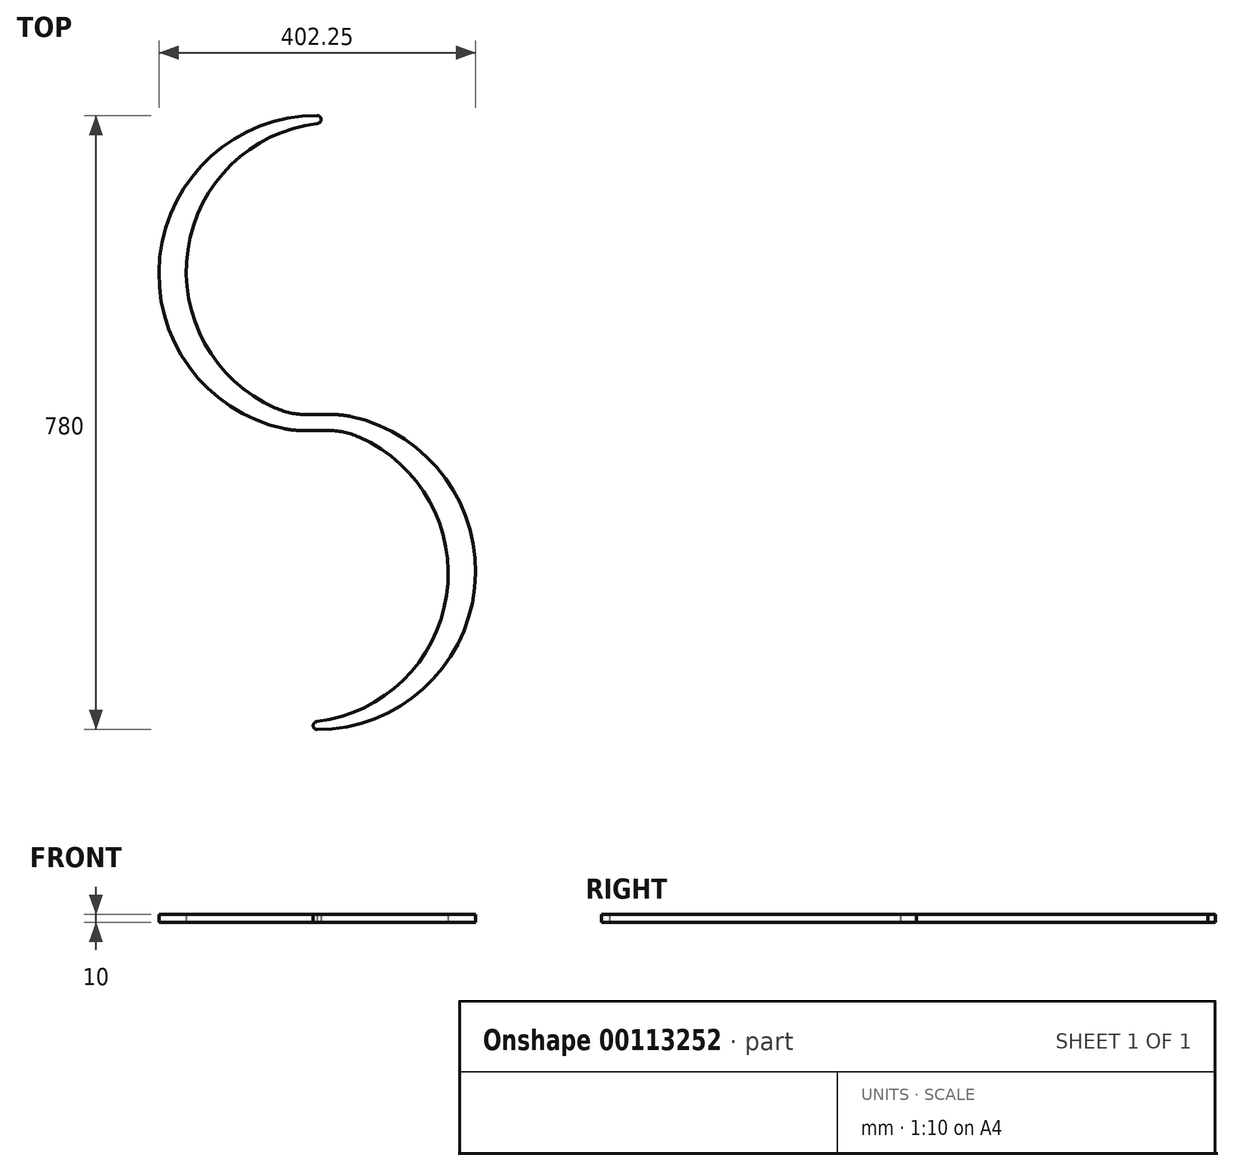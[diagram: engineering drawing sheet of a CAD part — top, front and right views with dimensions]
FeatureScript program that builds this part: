
annotation { "Feature Type Name" : "Feature", "Feature Type Description" : "" }
export const myFeature = defineFeature(function(context is Context, id is Id, definition is map)
    precondition{}
    {
        {
            var Q0;
            Q0=qCreatedBy(makeId("Top.planeOp"),FACE);
            var sketch = newSketch(context, id + "F0", { "sketchPlane" : qUnion([Q0])});
            skArc(sketch, "E0", {"start": v(0, 390) * mm, "mid": v(-200, 210.09) * mm, "end": v(-42.2, -7.78) * mm});
            skLineSegment(sketch, "E1", {"start": v(-21.21, -10) * mm, "end": v(0, -10) * mm});
            skLineSegment(sketch, "E2", {"start": v(0, -10) * mm, "end": v(0, 10) * mm, "construction": true});
            skPoint(sketch, "E3", {"position": v(0, 0) * mm});
            skLineSegment(sketch, "E4", {"start": v(0, 10) * mm, "end": v(-12.94, 10) * mm});
            skArc(sketch, "E5", {"start": v(0, 380) * mm, "mid": v(-164.3, 219.56) * mm, "end": v(-53.31, 18.51) * mm});
            skArc(sketch, "E6", {"start": v(0, 380) * mm, "mid": v(5, 385) * mm, "end": v(0, 390) * mm});
            skArc(sketch, "E7.1.0", {"start": v(0, -390) * mm, "mid": v(200, -210.09) * mm, "end": v(42.2, 7.78) * mm});
            skArc(sketch, "E7.1.1", {"start": v(0, -380) * mm, "mid": v(164.3, -219.56) * mm, "end": v(53.31, -18.51) * mm});
            skArc(sketch, "E7.1.2", {"start": v(0, -380) * mm, "mid": v(-5, -385) * mm, "end": v(0, -390) * mm});
            skLineSegment(sketch, "E7.1.3", {"start": v(0, -10) * mm, "end": v(12.94, -10) * mm});
            skLineSegment(sketch, "E7.1.4", {"start": v(21.21, 10) * mm, "end": v(0, 10) * mm});
            skPoint(sketch, "E8.visualSharp", {"position": v(-30, 10) * mm});
            skArc(sketch, "E8.filletArc", {"start": v(-53.31, 18.51) * mm, "mid": v(-33.57, 12.15) * mm, "end": v(-12.94, 10) * mm});
            skPoint(sketch, "E9.visualSharp", {"position": v(30, 10) * mm});
            skArc(sketch, "E9.filletArc", {"start": v(42.2, 7.78) * mm, "mid": v(31.76, 9.44) * mm, "end": v(21.21, 10) * mm});
            skPoint(sketch, "E10.visualSharp", {"position": v(-30, -10) * mm});
            skArc(sketch, "E10.filletArc", {"start": v(-42.2, -7.78) * mm, "mid": v(-31.76, -9.44) * mm, "end": v(-21.21, -10) * mm});
            skPoint(sketch, "E11.visualSharp", {"position": v(30, -10) * mm});
            skArc(sketch, "E11.filletArc", {"start": v(53.31, -18.51) * mm, "mid": v(33.57, -12.15) * mm, "end": v(12.94, -10) * mm});
            skLineSegment(sketch, "E12.bottom", {"start": v(47.12, -23.38) * mm, "end": v(-234.9, -23.38) * mm, "construction": true});
            skLineSegment(sketch, "E12.top", {"start": v(47.12, 411.9) * mm, "end": v(-234.9, 411.9) * mm, "construction": true});
            skLineSegment(sketch, "E12.left", {"start": v(47.12, -23.38) * mm, "end": v(47.12, 411.9) * mm, "construction": true});
            skLineSegment(sketch, "E12.right", {"start": v(-234.9, -23.38) * mm, "end": v(-234.9, 411.9) * mm, "construction": true});
            skSolve(sketch);
        }
        {
            var Q0;
            Q0 = qSketchRegion(id + "F0", true);
            extrude(context, id + "F1", {"entities" : qUnion([Q0]), "depth" : 10 * mm});
        }
    });
